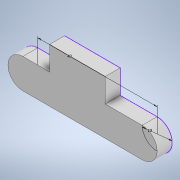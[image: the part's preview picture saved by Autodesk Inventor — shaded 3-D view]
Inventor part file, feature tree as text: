
AUTODESK INVENTOR PART (.ipt)
format: ipt  version: 2022 (Build 260153000, 153)  size: 104,960 bytes
history: native  units: mm
features: extrude x2, sketch x1
ambient origin geometry x8: Origin, YZ Plane, XZ Plane, XY Plane, X Axis, Y Axis, Z Axis, Center Point
bodies: Solid1 (feature_tree)
feature tree (3):
  sketch  "Sketch1"  dims[d0=10.0mm d2=40.0mm d3=5.0mm d4=0.0mm d7=5.0mm d8=0.0mm]
  extrude  "Extrusion1"  Depth=5.0mm
  extrude  "Extrusion3"  Depth=5.0mm TaperAngle=0.0deg
